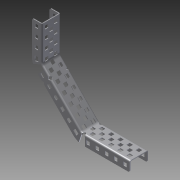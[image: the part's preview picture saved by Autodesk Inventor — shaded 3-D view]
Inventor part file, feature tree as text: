
AUTODESK INVENTOR PART (.ipt)
format: ipt  version: 2012 (Build 160160000, 160)  size: 1,581,056 bytes
history: native  units: in
note: dims shown in document units (in); Inventor stores cm internally (conversion verified against a paired STEP export)
features: sketch x4, other x3, extrude x2, imported_body x1
ambient origin geometry x8: Origin, YZ Plane, XZ Plane, XY Plane, X Axis, Y Axis, Z Axis, Center Point
feature tree (10):
  parser-record x1  (decoder bookkeeping rows leaked as tree rows — omitted from the tree; the rows remain in map.json)
  imported_body  "Base1"
  extrude  "Extrusion2"  Depth=1.0in TaperAngle=0.0deg
  extrude  "Extrusion3"  Depth=0.25in TaperAngle=45.0deg
  sketch  "Sketch8"
  sketch  "Sketch9"
  other  "Bend Part5"
  other  "Bend Part6"
  sketch  "Sketch2"  dims[d2=1.0in d3=0.0in d12=1.0in d13=0.0in]
  sketch  "Sketch7"  dims[d14=0.25in d15=45.0deg d16=0.25in d17=45.0deg]
